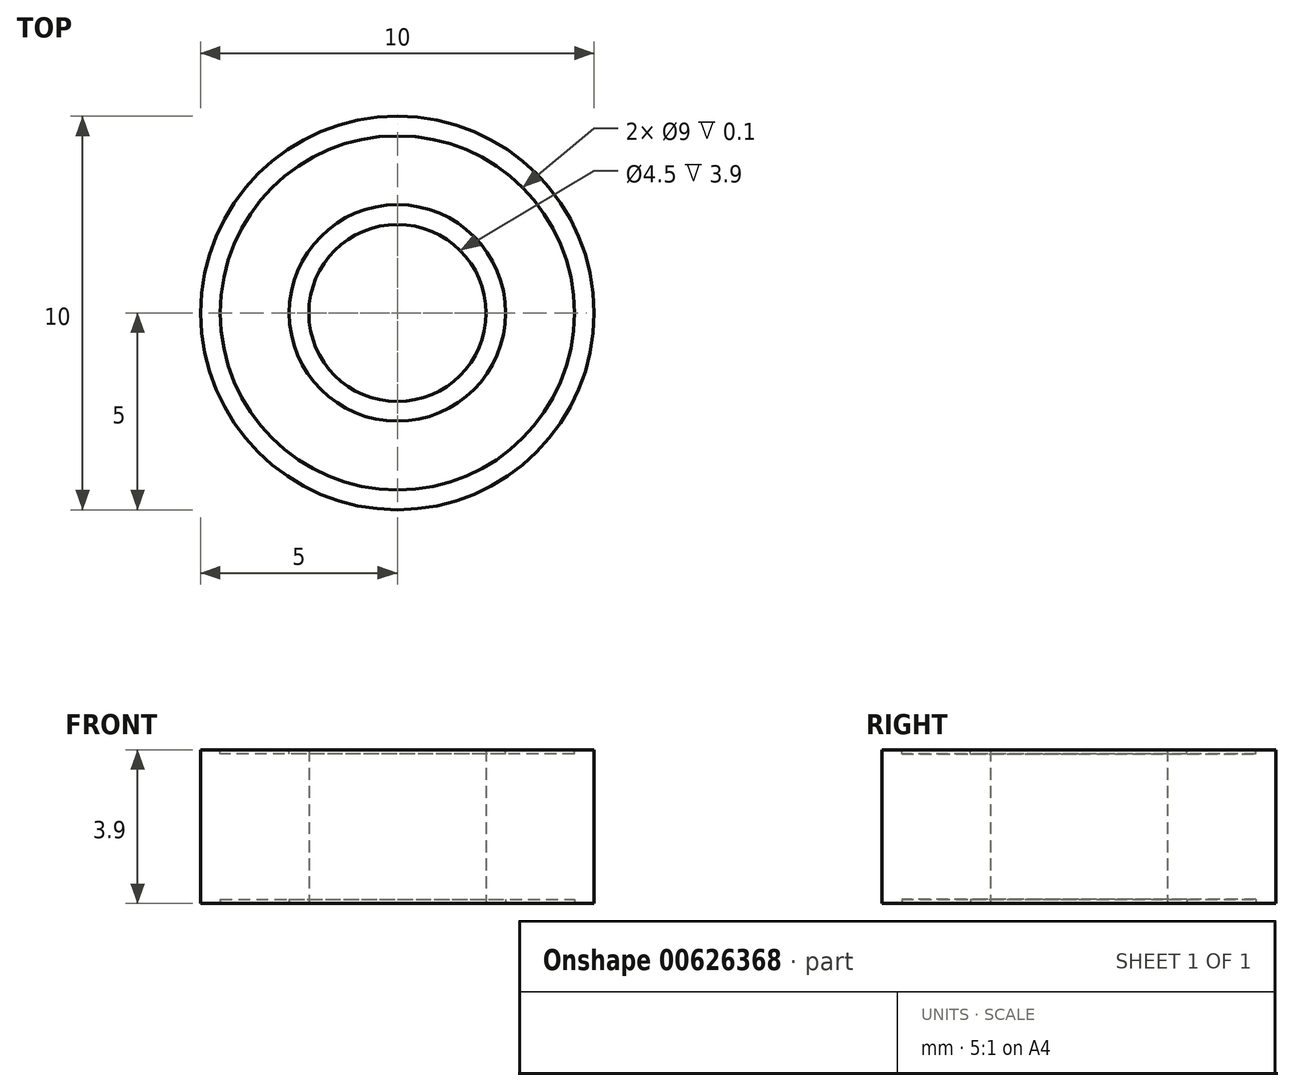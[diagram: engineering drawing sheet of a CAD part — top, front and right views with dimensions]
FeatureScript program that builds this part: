
annotation { "Feature Type Name" : "Feature", "Feature Type Description" : "" }
export const myFeature = defineFeature(function(context is Context, id is Id, definition is map)
    precondition{}
    {
        {
            var Q0;
            Q0=qCreatedBy(makeId("Top.planeOp"),FACE);
            var sketch = newSketch(context, id + "F0", { "sketchPlane" : qUnion([Q0])});
            skCircle(sketch, "E0", {"center": v(0, 0) * mm, "radius": 5 * mm});
            skCircle(sketch, "E1", {"center": v(0, 0) * mm, "radius": 2.25 * mm});
            skSolve(sketch);
        }
        {
            var Q0;
            Q0 = qSketchRegion(id + "F0", true);
            extrude(context, id + "F1", {"entities" : qUnion([Q0]), "depth" : 3.9 * mm, "offsetDistance" : 25 * mm});
        }
        {
            var Q0;
            Q0=makeQuery(id+"F1.opExtrude","CAP_FACE",FACE,{"disambiguationData":[OSD([sQuery(id+"F0.wireOp",EDGE,"E0"),sQuery(id+"F0.wireOp",EDGE,"E1")])],"isStart":false});
            var sketch = newSketch(context, id + "F2", { "sketchPlane" : qUnion([Q0])});
            skCircle(sketch, "E2", {"center": v(0, 0) * mm, "radius": 2.75 * mm});
            skCircle(sketch, "E3", {"center": v(0, 0) * mm, "radius": 4.5 * mm});
            skSolve(sketch);
        }
        {
            var Q0;
            Q0 = qSketchRegion(id + "F2", true);
            extrude(context, id + "F3", {"entities" : qUnion([Q0]), "operationType" : NewBodyOperationType.REMOVE, "oppositeDirection" : true, "depth" : 0.1 * mm, "offsetDistance" : 25 * mm});
        }
        {
            var Q0;
            Q0=makeQuery(id+"F1.opExtrude","CAP_FACE",FACE,{"disambiguationData":[OSD([sQuery(id+"F0.wireOp",EDGE,"E0"),sQuery(id+"F0.wireOp",EDGE,"E1")])],"isStart":true});
            var sketch = newSketch(context, id + "F4", { "sketchPlane" : qUnion([Q0])});
            skCircle(sketch, "E4", {"center": v(0, 0) * mm, "radius": 2.75 * mm});
            skCircle(sketch, "E5", {"center": v(0, 0) * mm, "radius": 4.5 * mm});
            skSolve(sketch);
        }
        {
            var Q0;
            Q0 = qSketchRegion(id + "F4", true);
            extrude(context, id + "F5", {"entities" : qUnion([Q0]), "operationType" : NewBodyOperationType.REMOVE, "oppositeDirection" : true, "depth" : 0.1 * mm, "offsetDistance" : 25 * mm});
        }
    });
